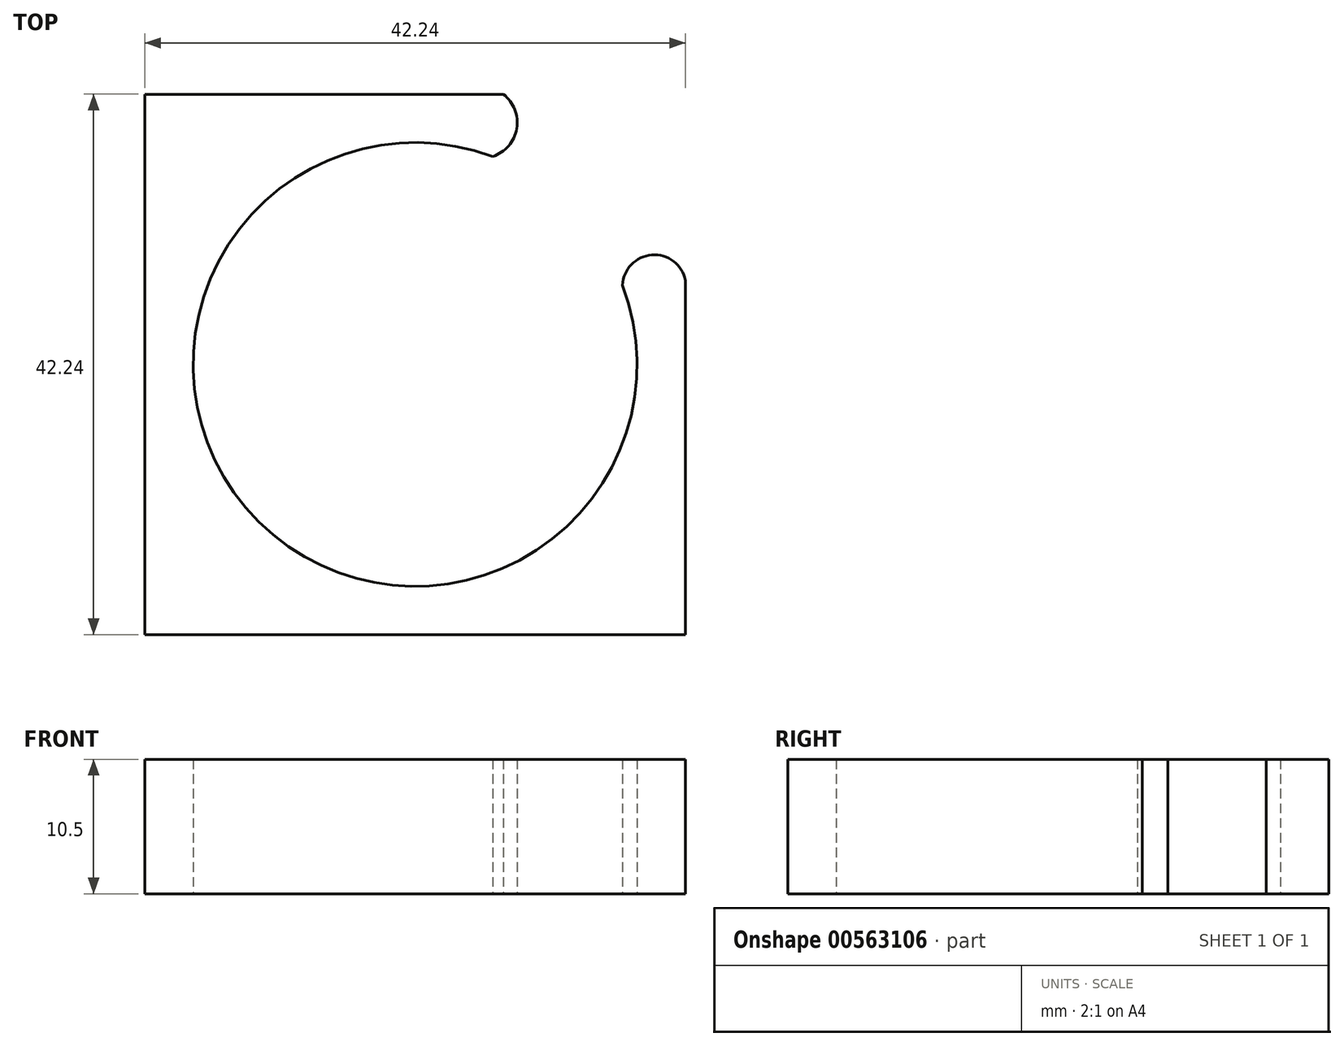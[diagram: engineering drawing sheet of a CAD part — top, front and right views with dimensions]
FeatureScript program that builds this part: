
annotation { "Feature Type Name" : "Feature", "Feature Type Description" : "" }
export const myFeature = defineFeature(function(context is Context, id is Id, definition is map)
    precondition{}
    {
        {
            var Q0;
            Q0=qCreatedBy(makeId("Top.planeOp"),FACE);
            var sketch = newSketch(context, id + "F0", { "sketchPlane" : qUnion([Q0])});
            skLineSegment(sketch, "E0.bottom", {"start": v(21.12, 21.12) * mm, "end": v(-21.12, 21.12) * mm});
            skLineSegment(sketch, "E0.top", {"start": v(21.12, -21.12) * mm, "end": v(-21.12, -21.12) * mm});
            skLineSegment(sketch, "E0.left", {"start": v(21.12, 21.12) * mm, "end": v(21.12, -21.12) * mm});
            skLineSegment(sketch, "E0.right", {"start": v(-21.12, 21.12) * mm, "end": v(-21.12, -21.12) * mm});
            skPoint(sketch, "E0.middle", {"position": v(0, 0) * mm});
            skCircle(sketch, "E1", {"center": v(0, 0) * mm, "radius": 17.34 * mm});
            skArc(sketch, "E2", {"start": v(6.06, 16.24) * mm, "mid": v(7.93, 18.43) * mm, "end": v(6.9, 21.12) * mm});
            skArc(sketch, "E3", {"start": v(21.12, 6.57) * mm, "mid": v(18.49, 8.56) * mm, "end": v(16.2, 6.19) * mm});
            skSolve(sketch);
        }
        {
            var Q0;
            {var subQ2=sQuery(id+"F0.wireOp",EDGE,"E0.top");Q0=makeQuery(id+"F0.imprint","IMPRINT",FACE,{"disambiguationData":[TD([[makeQuery(id+"F0.imprint","IMPRINT",EDGE,{"derivedFrom":subQ2}),-1.0]])]});}
            extrude(context, id + "F1", {"entities" : qUnion([Q0]), "depth" : 10.5 * mm, "offsetDistance" : 25 * mm});
        }
    });
